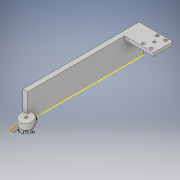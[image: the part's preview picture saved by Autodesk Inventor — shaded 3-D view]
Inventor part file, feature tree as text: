
AUTODESK INVENTOR PART (.ipt)
format: ipt  version: 2017 (Build 210142000, 142)  size: 189,440 bytes
history: native  units: in
note: dims shown in document units (in); Inventor stores cm internally (conversion verified against a paired STEP export)
features: sketch x8, projected_geometry x7, extrude x4, hole x3, plane x1
ambient origin geometry x8: Origin, YZ Plane, XZ Plane, XY Plane, X Axis, Y Axis, Z Axis, Center Point
bodies: Body1 (feature_tree)
feature tree (23):
  extrude  "Extrusion2"  Depth=4.5in
  sketch  "Sketch3"  dims[d8=0.1875in d9=0.0in d10=1.1681in]
  plane  "Work Plane1"
  sketch  "Sketch4"  dims[d18=0.125in d19=0.0in d28=0.5in]
  extrude  "Extrusion4"  Depth=0.1875in
  extrude  "Extrusion6"  Depth=0.125in
  extrude  "Extrusion9"  Depth=0.1875in
  hole  "Hole1"  [1 undecoded]
  hole  "Hole2"  [1 undecoded]
  hole  "Hole3"  [1 undecoded]
  sketch  "Sketch2"  dims[d6=1.0in d7=4.5in]
  projected_geometry  "Projected Loop1"
  sketch  "Sketch5"  dims[d29=0.1875in d30=0.0625in]
  projected_geometry  "Projected Loop2"
  sketch  "Sketch10"  dims[d32=0.25in d33=0.0in d40=0.075in]
  projected_geometry  "Projected Loop8"
  projected_geometry  "Projected Loop9"
  sketch  "Sketch11"  dims[d41=0.4846in d42=0.2423in]
  projected_geometry  "Projected Loop10"
  sketch  "Sketch12"  dims[d43=0.6871in d44=0.35in]
  projected_geometry  "Projected Loop11"
  sketch  "Sketch13"  dims[d45=0.1in d46=0.0in d47=1.3125in d48=0.1875in d49=0.75in d50=0.6299in d53=0.75in d54=1.125in d55=0.375in d56=0.315in d57=0.1575in d58=0.625in d59=0.115in d60=0.75in d61=0.375in d62=0.25in d63=0.5635in d64=1.0in d65=0.8108in d66=0.1in d67=0.75in d68=0.375in d69=0.25in d70=0.5635in d71=1.0in d72=0.8108in d73=0.1in d74=0.75in d75=0.375in d76=0.25in d77=0.5635in d78=1.0in d79=0.8108in]
  projected_geometry  "Projected Loop12"
note: 3 required parameter values undecoded (feature->parameter linkage not recoverable at this tier; creation-order binding heuristic only, values carry confidence <= 0.55)
